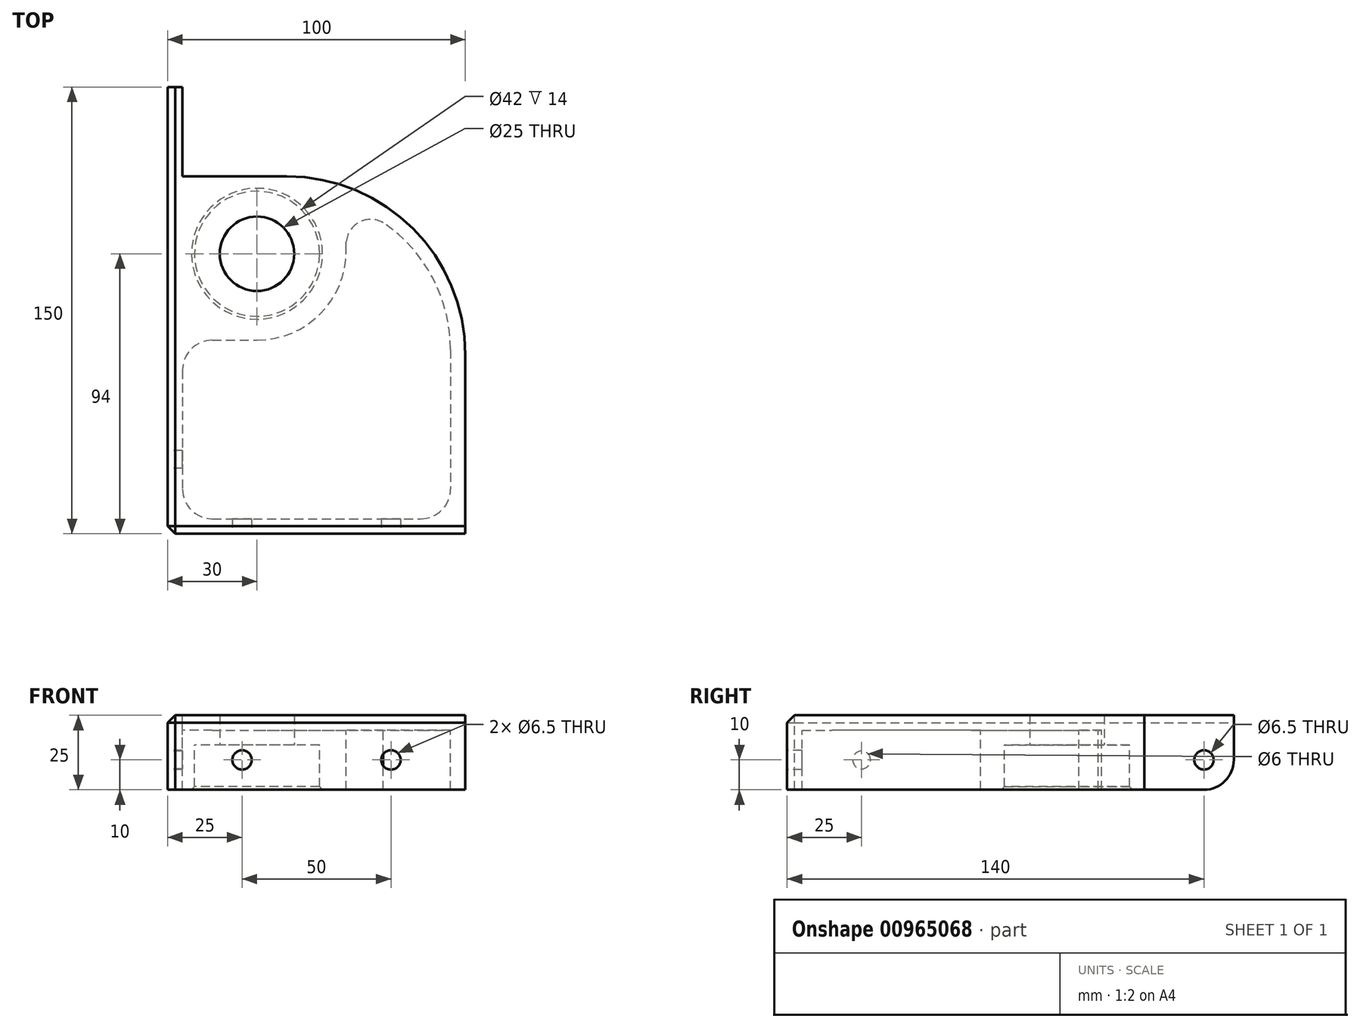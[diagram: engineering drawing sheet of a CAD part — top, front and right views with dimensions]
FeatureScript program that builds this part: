
annotation { "Feature Type Name" : "Feature", "Feature Type Description" : "" }
export const myFeature = defineFeature(function(context is Context, id is Id, definition is map)
    precondition{}
    {
        {
            var Q0;
            Q0=qCreatedBy(makeId("Top.planeOp"),FACE);
            var sketch = newSketch(context, id + "F0", { "sketchPlane" : qUnion([Q0])});
            skLineSegment(sketch, "E0", {"start": v(0, 0) * mm, "end": v(0, 120) * mm});
            skLineSegment(sketch, "E1", {"start": v(100, 0) * mm, "end": v(0, 0) * mm});
            skLineSegment(sketch, "E2", {"start": v(0, 120) * mm, "end": v(5, 120) * mm});
            skLineSegment(sketch, "E3", {"start": v(100, 5) * mm, "end": v(100, 0) * mm});
            skLineSegment(sketch, "E4", {"start": v(5, 120) * mm, "end": v(5, 5) * mm});
            skLineSegment(sketch, "E5", {"start": v(5, 5) * mm, "end": v(100, 5) * mm});
            skLineSegment(sketch, "E6", {"start": v(5, 120) * mm, "end": v(40, 120) * mm});
            skLineSegment(sketch, "E7", {"start": v(100, 60) * mm, "end": v(100, 5) * mm});
            skPoint(sketch, "E8.center", {"position": v(30, 87) * mm});
            skPoint(sketch, "E9.visualSharp", {"position": v(100, 120) * mm});
            skArc(sketch, "E9.filletArc", {"start": v(100, 60) * mm, "mid": v(82.43, 102.43) * mm, "end": v(40, 120) * mm});
            skLineSegment(sketch, "E10", {"start": v(-20, -20) * mm, "end": v(-20, 140) * mm, "construction": true});
            skLineSegment(sketch, "E11", {"start": v(-20, 140) * mm, "end": v(0, 140) * mm, "construction": true});
            skLineSegment(sketch, "E12", {"start": v(-10, -167) * mm, "end": v(-10, 160.54) * mm, "construction": true});
            skLineSegment(sketch, "E13", {"start": v(-27.5, -172.08) * mm, "end": v(-27.5, -121.08) * mm, "construction": true});
            skLineSegment(sketch, "E14", {"start": v(-27.5, -121.08) * mm, "end": v(37.5, -121.08) * mm, "construction": true});
            skLineSegment(sketch, "E15", {"start": v(37.5, -121.08) * mm, "end": v(37.5, -127.08) * mm, "construction": true});
            skLineSegment(sketch, "E16", {"start": v(37.5, -127.08) * mm, "end": v(7.5, -127.08) * mm, "construction": true});
            skLineSegment(sketch, "E17", {"start": v(7.5, -127.08) * mm, "end": v(7.5, -172.08) * mm, "construction": true});
            skLineSegment(sketch, "E18", {"start": v(7.5, -172.08) * mm, "end": v(2.5, -172.08) * mm, "construction": true});
            skLineSegment(sketch, "E19", {"start": v(2.5, -172.08) * mm, "end": v(2.5, -127.08) * mm, "construction": true});
            skLineSegment(sketch, "E20", {"start": v(2.5, -127.08) * mm, "end": v(-22.5, -127.08) * mm, "construction": true});
            skLineSegment(sketch, "E21", {"start": v(-22.5, -127.08) * mm, "end": v(-22.5, -172.08) * mm, "construction": true});
            skLineSegment(sketch, "E22", {"start": v(-22.5, -172.08) * mm, "end": v(-27.5, -172.08) * mm, "construction": true});
            skPoint(sketch, "E23", {"position": v(-10, -147.08) * mm});
            skPoint(sketch, "E24", {"position": v(30, -51.08) * mm});
            skLineSegment(sketch, "E25", {"start": v(0, 140) * mm, "end": v(0, 0) * mm, "construction": true});
            skLineSegment(sketch, "E26", {"start": v(140, 0) * mm, "end": v(140, -20) * mm, "construction": true});
            skLineSegment(sketch, "E27", {"start": v(140, 0) * mm, "end": v(0, 0) * mm, "construction": true});
            skLineSegment(sketch, "E28", {"start": v(-20, -20) * mm, "end": v(140, -20) * mm, "construction": true});
            skLineSegment(sketch, "E29", {"start": v(-50.25, -10) * mm, "end": v(191.36, -10) * mm, "construction": true});
            skPoint(sketch, "E30", {"position": v(30, 94) * mm});
            skCircle(sketch, "E31", {"center": v(30, 94) * mm, "radius": 12.5 * mm});
            skCircle(sketch, "E32", {"center": v(30, 94) * mm, "radius": 21 * mm});
            skLineSegment(sketch, "E33", {"start": v(5, 65) * mm, "end": v(30, 65) * mm});
            skLineSegment(sketch, "E34", {"start": v(60, 95) * mm, "end": v(60, 98) * mm});
            skArc(sketch, "E35", {"start": v(72.44, 104.41) * mm, "mid": v(64.44, 104.65) * mm, "end": v(60, 98) * mm});
            skArc(sketch, "E36", {"start": v(95, 61.84) * mm, "mid": v(89.01, 85.93) * mm, "end": v(72.44, 104.41) * mm});
            skLineSegment(sketch, "E37", {"start": v(95, 61.84) * mm, "end": v(95, 5) * mm});
            skPoint(sketch, "E38.visualSharp", {"position": v(60, 65) * mm});
            skArc(sketch, "E38.filletArc", {"start": v(30, 65) * mm, "mid": v(51.21, 73.79) * mm, "end": v(60, 95) * mm});
            skSolve(sketch);
        }
        {
            var Q0;
            Q0=makeQuery(id+"F0.imprint","IMPRINT",FACE,{"disambiguationData":[TD([[makeQuery(id+"F0.imprint","IMPRINT",EDGE,{"derivedFrom":sQuery(id+"F0.wireOp",EDGE,"E0")}),-1.0]])]});
            var Q1;
            Q1=makeQuery(id+"F0.imprint","IMPRINT",FACE,{"disambiguationData":[TD([[makeQuery(id+"F0.imprint","IMPRINT",EDGE,{"derivedFrom":sQuery(id+"F0.wireOp",EDGE,"ppYuwMZk-ploc-tXMn-lUmO-auRrpxJ4f4xt")}),-1.0]])]});
            var Q2;
            Q2=makeQuery(id+"F0.imprint","IMPRINT",FACE,{"disambiguationData":[TD([[makeQuery(id+"F0.imprint","IMPRINT",EDGE,{"derivedFrom":sQuery(id+"F0.wireOp",EDGE,"E4")}),1.0]])]});
            var Q3;
            {var subQ0=sQuery(id+"F0.wireOp",EDGE,"PSJROaDc-Aqwe-zX3O-wr75-Hd8r8wIWMBKI.bottom");Q3=makeQuery(id+"F0.imprint","IMPRINT",FACE,{"disambiguationData":[TD([[makeQuery(id+"F0.imprint","IMPRINT",EDGE,{"derivedFrom":subQ0}),-1.0]])]});}
            var Q4;
            Q4=makeQuery(id+"F0.imprint","IMPRINT",FACE,{"disambiguationData":[TD([[makeQuery(id+"F0.imprint","IMPRINT",EDGE,{"derivedFrom":sQuery(id+"F0.wireOp",EDGE,"NLFgxsRY-dQg0-scZF-8bRf-c5N5ptYbvfvn.top")}),-1.0]])]});
            var Q5;
            {var subQ3=sQuery(id+"F0.wireOp",EDGE,"ZZHPZ1UJ-gQvc-y5dD-WxQZ-NW3lf6L0Z9ZP.top");Q5=makeQuery(id+"F0.imprint","IMPRINT",FACE,{"disambiguationData":[TD([[makeQuery(id+"F0.imprint","IMPRINT",EDGE,{"derivedFrom":subQ3}),1.0]])]});}
            var Q6;
            Q6=makeQuery(id+"F0.imprint","IMPRINT",FACE,{"disambiguationData":[TD([[makeQuery(id+"F0.imprint","IMPRINT",EDGE,{"derivedFrom":sQuery(id+"F0.wireOp",EDGE,"E31")}),-1.0]])]});
            var Q7;
            Q7=makeQuery(id+"F0.imprint","IMPRINT",FACE,{"disambiguationData":[TD([[makeQuery(id+"F0.imprint","IMPRINT",EDGE,{"derivedFrom":sQuery(id+"F0.wireOp",EDGE,"E32")}),-1.0]])]});
            extrude(context, id + "F1", {"entities" : qUnion([Q0, Q1, Q2, Q3, Q4, Q5, Q6, Q7]), "depth" : 5 * mm, "offsetDistance" : 25 * mm});
        }
        {
            var Q0;
            Q0=makeQuery(id+"F0.imprint","IMPRINT",FACE,{"disambiguationData":[TD([[makeQuery(id+"F0.imprint","IMPRINT",EDGE,{"derivedFrom":sQuery(id+"F0.wireOp",EDGE,"E0")}),-1.0]])]});
            var Q1;
            {var subQ0=sQuery(id+"F0.wireOp",EDGE,"PSJROaDc-Aqwe-zX3O-wr75-Hd8r8wIWMBKI.bottom");Q1=makeQuery(id+"F0.imprint","IMPRINT",FACE,{"disambiguationData":[TD([[makeQuery(id+"F0.imprint","IMPRINT",EDGE,{"derivedFrom":subQ0}),-1.0]])]});}
            var Q2;
            Q2=makeQuery(id+"F0.imprint","IMPRINT",FACE,{"disambiguationData":[TD([[makeQuery(id+"F0.imprint","IMPRINT",EDGE,{"derivedFrom":sQuery(id+"F0.wireOp",EDGE,"NLFgxsRY-dQg0-scZF-8bRf-c5N5ptYbvfvn.top")}),-1.0]])]});
            var Q3;
            {var subQ3=sQuery(id+"F0.wireOp",EDGE,"ZZHPZ1UJ-gQvc-y5dD-WxQZ-NW3lf6L0Z9ZP.top");Q3=makeQuery(id+"F0.imprint","IMPRINT",FACE,{"disambiguationData":[TD([[makeQuery(id+"F0.imprint","IMPRINT",EDGE,{"derivedFrom":subQ3}),1.0]])]});}
            var Q4;
            {var subQ1=sQuery(id+"F0.wireOp",EDGE,"E6");Q4=makeQuery(id+"F0.imprint","IMPRINT",FACE,{"disambiguationData":[TD([[makeQuery(id+"F0.imprint","IMPRINT",EDGE,{"derivedFrom":subQ1}),-1.0]])]});}
            extrude(context, id + "F2", {"entities" : qUnion([Q0, Q1, Q2, Q3, Q4]), "operationType" : NewBodyOperationType.ADD, "flatOperationType" : FlatOperationType.REMOVE, "oppositeDirection" : true, "depth" : 20 * mm, "offsetDistance" : 25 * mm, "domain" : OperationDomain.MODEL});
        }
        {
            var Q0;
            {var subQ0=sQuery(id+"F0.wireOp",EDGE,"E6");var subQ1=sQuery(id+"F0.wireOp",EDGE,"E2");Q0=makeQuery(id+"F2.boolean.opBoolean","MERGE",FACE,{"derivedFrom":[makeQuery(id+"F1.opExtrude","SWEPT_FACE",FACE,{"disambiguationData":[OSD([subQ1,subQ0])]}),makeQuery(id+"F2.opExtrude","SWEPT_FACE",FACE,{"disambiguationData":[OSD([subQ1,subQ0])]})]});}
            var sketch = newSketch(context, id + "F3", { "sketchPlane" : qUnion([Q0])});
            skLineSegment(sketch, "E39.bottom", {"start": v(0, -20) * mm, "end": v(-5, -20) * mm});
            skLineSegment(sketch, "E39.top", {"start": v(0, 5) * mm, "end": v(-5, 5) * mm});
            skLineSegment(sketch, "E39.left", {"start": v(0, -20) * mm, "end": v(0, 5) * mm});
            skLineSegment(sketch, "E39.right", {"start": v(-5, -20) * mm, "end": v(-5, 5) * mm});
            skSolve(sketch);
        }
        {
            var Q0;
            {var subQ1=sQuery(id+"F3.wireOp",EDGE,"E39.bottom");Q0=makeQuery(id+"F3.imprint","IMPRINT",FACE,{"disambiguationData":[TD([[makeQuery(id+"F3.imprint","IMPRINT",EDGE,{"derivedFrom":subQ1}),-1.0]])]});}
            extrude(context, id + "F4", {"entities" : qUnion([Q0]), "operationType" : NewBodyOperationType.ADD, "depth" : 30 * mm, "offsetDistance" : 25 * mm});
        }
        {
            var Q0;
            {var subQ0=sQuery(id+"F0.wireOp",EDGE,"E0");Q0=makeQuery(id+"F2.boolean.opBoolean","MERGE",FACE,{"derivedFrom":[makeQuery(id+"F1.opExtrude","SWEPT_FACE",FACE,{"disambiguationData":[OSD([subQ0])]}),makeQuery(id+"F2.opExtrude","SWEPT_FACE",FACE,{"disambiguationData":[OSD([subQ0])]})]});}
            var sketch = newSketch(context, id + "F5", { "sketchPlane" : qUnion([Q0])});
            skCircle(sketch, "E40", {"center": v(-140, -10) * mm, "radius": 3.25 * mm});
            skCircle(sketch, "E41", {"center": v(-25, -10) * mm, "radius": 3 * mm});
            skSolve(sketch);
        }
        {
            var Q0;
            {var subQ0=sQuery(id+"F0.wireOp",EDGE,"E1");Q0=makeQuery(id+"F2.boolean.opBoolean","MERGE",FACE,{"derivedFrom":[makeQuery(id+"F1.opExtrude","SWEPT_FACE",FACE,{"disambiguationData":[OSD([subQ0])]}),makeQuery(id+"F2.opExtrude","SWEPT_FACE",FACE,{"disambiguationData":[OSD([subQ0])]})]});}
            var sketch = newSketch(context, id + "F6", { "sketchPlane" : qUnion([Q0])});
            skCircle(sketch, "E42", {"center": v(25, -10) * mm, "radius": 3.25 * mm});
            skCircle(sketch, "E43", {"center": v(75, -10) * mm, "radius": 3.25 * mm});
            skSolve(sketch);
        }
        {
            var Q0;
            Q0=makeQuery(id+"F6.imprint","IMPRINT",FACE,{"disambiguationData":[TD([[makeQuery(id+"F6.imprint","IMPRINT",EDGE,{"derivedFrom":sQuery(id+"F6.wireOp",EDGE,"E42")}),1.0]])]});
            var Q1;
            Q1=makeQuery(id+"F6.imprint","IMPRINT",FACE,{"disambiguationData":[TD([[makeQuery(id+"F6.imprint","IMPRINT",EDGE,{"derivedFrom":sQuery(id+"F6.wireOp",EDGE,"E43")}),1.0]])]});
            extrude(context, id + "F7", {"entities" : qUnion([Q0, Q1]), "operationType" : NewBodyOperationType.REMOVE, "oppositeDirection" : true, "depth" : 25 * mm, "offsetDistance" : 25 * mm});
        }
        {
            var Q0;
            Q0=makeQuery(id+"F5.imprint","IMPRINT",FACE,{"disambiguationData":[TD([[makeQuery(id+"F5.imprint","IMPRINT",EDGE,{"derivedFrom":sQuery(id+"F5.wireOp",EDGE,"E41")}),1.0]])]});
            var Q1;
            Q1=makeQuery(id+"F5.imprint","IMPRINT",FACE,{"disambiguationData":[TD([[makeQuery(id+"F5.imprint","IMPRINT",EDGE,{"derivedFrom":sQuery(id+"F5.wireOp",EDGE,"E40")}),1.0]])]});
            extrude(context, id + "F8", {"entities" : qUnion([Q0, Q1]), "operationType" : NewBodyOperationType.REMOVE, "oppositeDirection" : true, "depth" : 25 * mm, "offsetDistance" : 25 * mm});
        }
        {
            var Q0;
            Q0=makeQuery(id+"F1.opExtrude","CAP_EDGE",EDGE,{"disambiguationData":[OSD([sQuery(id+"F0.wireOp",EDGE,"E1")])],"isStart":false});
            var Q1;
            Q1=makeQuery(id+"F1.opExtrude","CAP_EDGE",EDGE,{"disambiguationData":[OSD([sQuery(id+"F0.wireOp",EDGE,"E0")])],"isStart":false});
            var Q2;
            {var subQ0=sQuery(id+"F0.wireOp",EDGE,"E1");var subQ1=sQuery(id+"F0.wireOp",EDGE,"E0");Q2=makeQuery(id+"F2.boolean.opBoolean","MERGE",EDGE,{"derivedFrom":[makeQuery(id+"F1.opExtrude","SWEPT_EDGE",EDGE,{"disambiguationData":[OSD([subQ1,subQ0])]}),makeQuery(id+"F2.opExtrude","SWEPT_EDGE",EDGE,{"disambiguationData":[OSD([subQ1,subQ0])]})]});}
            chamfer(context, id + "F9", {"entities" : qUnion([Q0, Q1, Q2]), "width" : 2.5 * mm, "tangentPropagation" : true});
        }
        {
            var Q0;
            Q0=makeQuery(id+"F2.opExtrude","SWEPT_EDGE",EDGE,{"disambiguationData":[OSD([sQuery(id+"F0.wireOp",EDGE,"E4"),sQuery(id+"F0.wireOp",EDGE,"E5")])]});
            var Q1;
            Q1=makeQuery(id+"F2.opExtrude","SWEPT_EDGE",EDGE,{"disambiguationData":[OSD([sQuery(id+"F0.wireOp",EDGE,"E5"),sQuery(id+"F0.wireOp",EDGE,"E37")])]});
            var Q2;
            Q2=makeQuery(id+"F2.opExtrude","SWEPT_EDGE",EDGE,{"disambiguationData":[OSD([sQuery(id+"F0.wireOp",EDGE,"E4"),sQuery(id+"F0.wireOp",EDGE,"E33")])]});
            var Q3;
            Q3=makeQuery(id+"F4.opExtrude","CAP_EDGE",EDGE,{"disambiguationData":[OSD([sQuery(id+"F3.wireOp",EDGE,"E39.right")])],"isStart":true});
            var Q4;
            Q4=makeQuery(id+"F4.opExtrude","CAP_EDGE",EDGE,{"disambiguationData":[OSD([sQuery(id+"F3.wireOp",EDGE,"E39.bottom")])],"isStart":false});
            fillet(context, id + "F10", {"entities" : qUnion([Q0, Q1, Q2, Q3, Q4]), "tangentPropagation" : true, "radius" : 10 * mm, "defaultsChanged" : true, "vertexSettings" : [], "allowEdgeOverflow" : false});
        }
        {
            var Q0;
            Q0=makeQuery(id+"F0.imprint","IMPRINT",FACE,{"disambiguationData":[TD([[makeQuery(id+"F0.imprint","IMPRINT",EDGE,{"derivedFrom":sQuery(id+"F0.wireOp",EDGE,"E31")}),-1.0]])]});
            extrude(context, id + "F11", {"entities" : qUnion([Q0]), "operationType" : NewBodyOperationType.ADD, "oppositeDirection" : true, "depth" : 5 * mm, "offsetDistance" : 25 * mm});
        }
        {
            var Q0;
            Q0=makeQuery(id+"F2.opExtrude","CAP_EDGE",EDGE,{"disambiguationData":[OSD([sQuery(id+"F0.wireOp",EDGE,"E32")])],"isStart":false});
            chamfer(context, id + "F12", {"entities" : qUnion([Q0]), "width" : 1 * mm, "tangentPropagation" : true});
        }
    });
